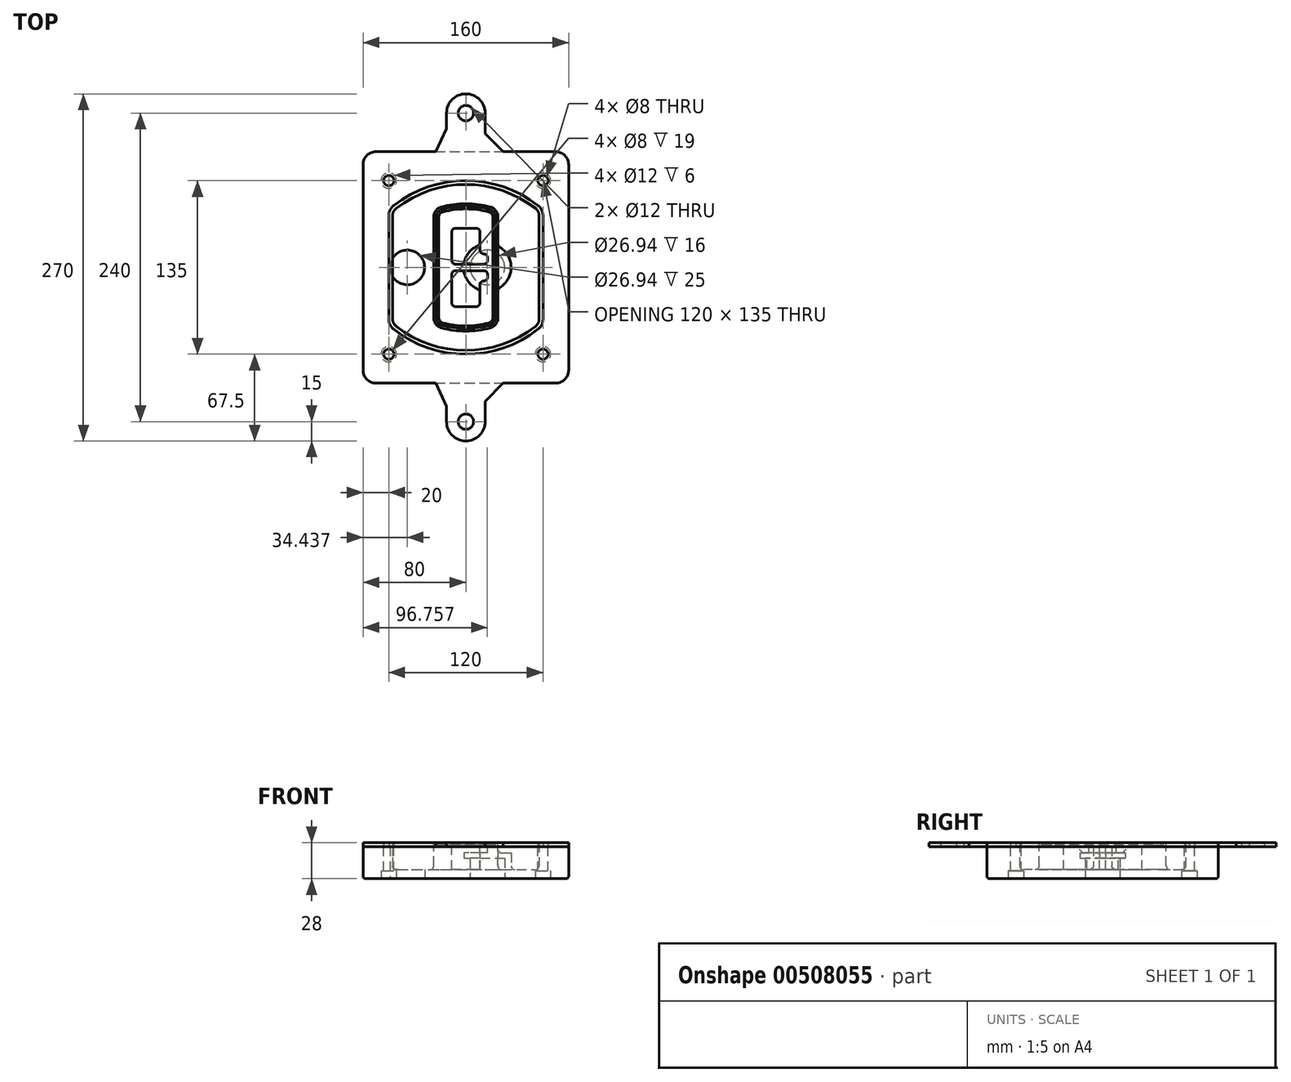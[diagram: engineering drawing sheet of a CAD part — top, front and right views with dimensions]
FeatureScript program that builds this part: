
annotation { "Feature Type Name" : "Feature", "Feature Type Description" : "" }
export const myFeature = defineFeature(function(context is Context, id is Id, definition is map)
    precondition{}
    {
        {
            var Q0;
            Q0=qCreatedBy(makeId("Top.planeOp"),FACE);
            var sketch = newSketch(context, id + "F0", { "sketchPlane" : qUnion([Q0])});
            skPoint(sketch, "E0.rect.middle", {"position": v(0, 0) * mm});
            skLineSegment(sketch, "E1.bottom", {"start": v(-70, -90) * mm, "end": v(70, -90) * mm});
            skLineSegment(sketch, "E1.top", {"start": v(-70, 90) * mm, "end": v(70, 90) * mm});
            skLineSegment(sketch, "E1.left", {"start": v(-80, -80) * mm, "end": v(-80, 80) * mm});
            skLineSegment(sketch, "E1.right", {"start": v(80, -80) * mm, "end": v(80, 80) * mm});
            skLineSegment(sketch, "E2", {"start": v(-80, 90) * mm, "end": v(80, -90) * mm, "construction": true});
            skLineSegment(sketch, "E3", {"start": v(80, 90) * mm, "end": v(-80, -90) * mm, "construction": true});
            skCircle(sketch, "E4", {"center": v(-60, 67.5) * mm, "radius": 4 * mm});
            skCircle(sketch, "E5", {"center": v(60, 67.5) * mm, "radius": 4 * mm});
            skCircle(sketch, "E6", {"center": v(60, -67.5) * mm, "radius": 4 * mm});
            skCircle(sketch, "E7", {"center": v(-60, -67.5) * mm, "radius": 4 * mm});
            skLineSegment(sketch, "E8", {"start": v(-60, 67.5) * mm, "end": v(60, 67.5) * mm, "construction": true});
            skLineSegment(sketch, "E9", {"start": v(60, 67.5) * mm, "end": v(60, -67.5) * mm, "construction": true});
            skLineSegment(sketch, "E10", {"start": v(60, -67.5) * mm, "end": v(-60, -67.5) * mm, "construction": true});
            skLineSegment(sketch, "E11", {"start": v(-60, -67.5) * mm, "end": v(-60, 67.5) * mm, "construction": true});
            skLineSegment(sketch, "E12", {"start": v(-60, 40.3) * mm, "end": v(-60, -40.3) * mm});
            skLineSegment(sketch, "E13", {"start": v(60, 40.3) * mm, "end": v(60, -40.3) * mm});
            skArc(sketch, "E14", {"start": v(56.15, 48.18) * mm, "mid": v(0, 67.5) * mm, "end": v(-56.15, 48.18) * mm});
            skArc(sketch, "E15", {"start": v(-56.15, -48.18) * mm, "mid": v(0, -67.5) * mm, "end": v(56.15, -48.18) * mm});
            skLineSegment(sketch, "E16", {"start": v(-60, 0) * mm, "end": v(60, 0) * mm, "construction": true});
            skPoint(sketch, "E17.visualSharp", {"position": v(-60, -45) * mm});
            skArc(sketch, "E17.filletArc", {"start": v(-60, -40.3) * mm, "mid": v(-58.99, -44.68) * mm, "end": v(-56.15, -48.18) * mm});
            skPoint(sketch, "E18.visualSharp", {"position": v(-60, 45) * mm});
            skArc(sketch, "E18.filletArc", {"start": v(-56.15, 48.18) * mm, "mid": v(-58.99, 44.68) * mm, "end": v(-60, 40.3) * mm});
            skPoint(sketch, "E19.visualSharp", {"position": v(60, 45) * mm});
            skArc(sketch, "E19.filletArc", {"start": v(60, 40.3) * mm, "mid": v(58.99, 44.68) * mm, "end": v(56.15, 48.18) * mm});
            skPoint(sketch, "E20.visualSharp", {"position": v(60, -45) * mm});
            skArc(sketch, "E20.filletArc", {"start": v(56.15, -48.18) * mm, "mid": v(58.99, -44.68) * mm, "end": v(60, -40.3) * mm});
            skPoint(sketch, "E21.visualSharp", {"position": v(-80, 90) * mm});
            skArc(sketch, "E21.filletArc", {"start": v(-70, 90) * mm, "mid": v(-77.07, 87.07) * mm, "end": v(-80, 80) * mm});
            skPoint(sketch, "E22.visualSharp", {"position": v(80, 90) * mm});
            skArc(sketch, "E22.filletArc", {"start": v(80, 80) * mm, "mid": v(77.07, 87.07) * mm, "end": v(70, 90) * mm});
            skPoint(sketch, "E23.visualSharp", {"position": v(80, -90) * mm});
            skArc(sketch, "E23.filletArc", {"start": v(70, -90) * mm, "mid": v(77.07, -87.07) * mm, "end": v(80, -80) * mm});
            skPoint(sketch, "E24.visualSharp", {"position": v(-80, -90) * mm});
            skArc(sketch, "E24.filletArc", {"start": v(-80, -80) * mm, "mid": v(-77.07, -87.07) * mm, "end": v(-70, -90) * mm});
            skArc(sketch, "E25.0", {"start": v(57, 40.3) * mm, "mid": v(56.3, 43.36) * mm, "end": v(54.3, 45.81) * mm});
            skLineSegment(sketch, "E25.1", {"start": v(57, 40.3) * mm, "end": v(57, -40.3) * mm});
            skArc(sketch, "E25.2", {"start": v(54.3, -45.81) * mm, "mid": v(56.3, -43.36) * mm, "end": v(57, -40.3) * mm});
            skArc(sketch, "E25.3", {"start": v(-54.3, -45.81) * mm, "mid": v(0, -64.5) * mm, "end": v(54.3, -45.81) * mm});
            skArc(sketch, "E25.4", {"start": v(-57, -40.3) * mm, "mid": v(-56.3, -43.36) * mm, "end": v(-54.3, -45.81) * mm});
            skArc(sketch, "E25.5", {"start": v(54.3, 45.81) * mm, "mid": v(0, 64.5) * mm, "end": v(-54.3, 45.81) * mm});
            skLineSegment(sketch, "E25.6", {"start": v(-57, 40.3) * mm, "end": v(-57, -40.3) * mm});
            skArc(sketch, "E25.7", {"start": v(-54.3, 45.81) * mm, "mid": v(-56.3, 43.36) * mm, "end": v(-57, 40.3) * mm});
            skArc(sketch, "E26.0", {"start": v(-58.62, 51.33) * mm, "mid": v(-62.58, 46.43) * mm, "end": v(-64, 40.3) * mm});
            skArc(sketch, "E26.1", {"start": v(58.62, 51.33) * mm, "mid": v(0, 71.5) * mm, "end": v(-58.62, 51.33) * mm});
            skArc(sketch, "E26.2", {"start": v(64, 40.3) * mm, "mid": v(62.58, 46.43) * mm, "end": v(58.62, 51.33) * mm});
            skLineSegment(sketch, "E26.3", {"start": v(64, 40.3) * mm, "end": v(64, -40.3) * mm});
            skArc(sketch, "E26.4", {"start": v(58.62, -51.33) * mm, "mid": v(62.58, -46.43) * mm, "end": v(64, -40.3) * mm});
            skLineSegment(sketch, "E26.5", {"start": v(-64, 40.3) * mm, "end": v(-64, -40.3) * mm});
            skArc(sketch, "E26.6", {"start": v(-58.62, -51.33) * mm, "mid": v(0, -71.5) * mm, "end": v(58.62, -51.33) * mm});
            skArc(sketch, "E26.7", {"start": v(-64, -40.3) * mm, "mid": v(-62.58, -46.43) * mm, "end": v(-58.62, -51.33) * mm});
            skSolve(sketch);
        }
        {
            var Q0;
            Q0=makeQuery(id+"F0.imprint","IMPRINT",FACE,{"disambiguationData":[TD([[makeQuery(id+"F0.imprint","IMPRINT",EDGE,{"derivedFrom":sQuery(id+"F0.wireOp",EDGE,"E1.bottom")}),1.0]])]});
            var Q1;
            Q1=makeQuery(id+"F0.imprint","IMPRINT",FACE,{"disambiguationData":[TD([[makeQuery(id+"F0.imprint","IMPRINT",EDGE,{"derivedFrom":sQuery(id+"F0.wireOp",EDGE,"E12")}),1.0]])]});
            var Q2;
            Q2=makeQuery(id+"F0.imprint","IMPRINT",FACE,{"disambiguationData":[TD([[makeQuery(id+"F0.imprint","IMPRINT",EDGE,{"derivedFrom":sQuery(id+"F0.wireOp",EDGE,"E25.0")}),1.0]])]});
            var Q3;
            Q3=makeQuery(id+"F0.imprint","IMPRINT",FACE,{"disambiguationData":[TD([[makeQuery(id+"F0.imprint","IMPRINT",EDGE,{"derivedFrom":sQuery(id+"F0.wireOp",EDGE,"E12")}),-1.0]])]});
            extrude(context, id + "F1", {"entities" : qUnion([Q0, Q1, Q2, Q3]), "oppositeDirection" : true, "depth" : 25 * mm});
        }
        {
            var Q0;
            Q0=makeQuery(id+"F0.imprint","IMPRINT",FACE,{"disambiguationData":[TD([[makeQuery(id+"F0.imprint","IMPRINT",EDGE,{"derivedFrom":sQuery(id+"F0.wireOp",EDGE,"E12")}),1.0]])]});
            extrude(context, id + "F2", {"entities" : qUnion([Q0]), "operationType" : NewBodyOperationType.ADD, "depth" : 3 * mm});
        }
        {
            var Q0;
            Q0=makeQuery(id+"F0.imprint","IMPRINT",FACE,{"disambiguationData":[TD([[makeQuery(id+"F0.imprint","IMPRINT",EDGE,{"derivedFrom":sQuery(id+"F0.wireOp",EDGE,"E25.0")}),1.0]])]});
            extrude(context, id + "F3", {"entities" : qUnion([Q0]), "operationType" : NewBodyOperationType.REMOVE, "oppositeDirection" : true, "depth" : 18 * mm});
        }
        {
            var Q0;
            Q0=makeQuery(id+"F2.opExtrude","CAP_FACE",FACE,{"disambiguationData":[OSD([sQuery(id+"F0.wireOp",EDGE,"E12"),sQuery(id+"F0.wireOp",EDGE,"E13"),sQuery(id+"F0.wireOp",EDGE,"E14"),sQuery(id+"F0.wireOp",EDGE,"E15"),sQuery(id+"F0.wireOp",EDGE,"E17.filletArc"),sQuery(id+"F0.wireOp",EDGE,"E18.filletArc"),sQuery(id+"F0.wireOp",EDGE,"E19.filletArc"),sQuery(id+"F0.wireOp",EDGE,"E20.filletArc"),sQuery(id+"F0.wireOp",EDGE,"E25.0"),sQuery(id+"F0.wireOp",EDGE,"E25.1"),sQuery(id+"F0.wireOp",EDGE,"E25.2"),sQuery(id+"F0.wireOp",EDGE,"E25.3"),sQuery(id+"F0.wireOp",EDGE,"E25.4"),sQuery(id+"F0.wireOp",EDGE,"E25.5"),sQuery(id+"F0.wireOp",EDGE,"E25.6"),sQuery(id+"F0.wireOp",EDGE,"E25.7")])],"isStart":false});
            var sketch = newSketch(context, id + "F4", { "sketchPlane" : qUnion([Q0])});
            skArc(sketch, "E27.0", {"start": v(-19.08, -46.97) * mm, "mid": v(0, -49.5) * mm, "end": v(19.08, -46.97) * mm});
            skArc(sketch, "E28.0", {"start": v(19.08, 46.97) * mm, "mid": v(0, 49.5) * mm, "end": v(-19.08, 46.97) * mm});
            skLineSegment(sketch, "E29", {"start": v(-25, 39.25) * mm, "end": v(-25, -39.25) * mm});
            skLineSegment(sketch, "E30", {"start": v(25, 39.25) * mm, "end": v(25, -39.25) * mm});
            skLineSegment(sketch, "E31", {"start": v(-25, 45.1) * mm, "end": v(25, 45.1) * mm, "construction": true});
            skLineSegment(sketch, "E32", {"start": v(-25, -45.1) * mm, "end": v(25, -45.1) * mm, "construction": true});
            skPoint(sketch, "E33.visualSharp", {"position": v(-25, 45.1) * mm});
            skArc(sketch, "E33.filletArc", {"start": v(-19.08, 46.97) * mm, "mid": v(-23.35, 44.11) * mm, "end": v(-25, 39.25) * mm});
            skPoint(sketch, "E34.visualSharp", {"position": v(25, 45.1) * mm});
            skArc(sketch, "E34.filletArc", {"start": v(25, 39.25) * mm, "mid": v(23.35, 44.11) * mm, "end": v(19.08, 46.97) * mm});
            skPoint(sketch, "E35.visualSharp", {"position": v(25, -45.1) * mm});
            skArc(sketch, "E35.filletArc", {"start": v(19.08, -46.97) * mm, "mid": v(23.35, -44.11) * mm, "end": v(25, -39.25) * mm});
            skPoint(sketch, "E36.visualSharp", {"position": v(-25, -45.1) * mm});
            skArc(sketch, "E36.filletArc", {"start": v(-25, -39.25) * mm, "mid": v(-23.35, -44.11) * mm, "end": v(-19.08, -46.97) * mm});
            skArc(sketch, "E37.0", {"start": v(54.3, 45.81) * mm, "mid": v(0, 64.5) * mm, "end": v(-54.3, 45.81) * mm});
            skArc(sketch, "E37.1", {"start": v(-54.3, 45.81) * mm, "mid": v(-56.3, 43.36) * mm, "end": v(-57, 40.3) * mm});
            skLineSegment(sketch, "E37.2", {"start": v(-57, 40.3) * mm, "end": v(-57, -40.3) * mm});
            skArc(sketch, "E37.3", {"start": v(-57, -40.3) * mm, "mid": v(-56.3, -43.36) * mm, "end": v(-54.3, -45.81) * mm});
            skArc(sketch, "E37.4", {"start": v(-54.3, -45.81) * mm, "mid": v(0, -64.5) * mm, "end": v(54.3, -45.81) * mm});
            skArc(sketch, "E37.5", {"start": v(54.3, -45.81) * mm, "mid": v(56.3, -43.36) * mm, "end": v(57, -40.3) * mm});
            skLineSegment(sketch, "E37.6", {"start": v(57, 40.3) * mm, "end": v(57, -40.3) * mm});
            skArc(sketch, "E37.7", {"start": v(57, 40.3) * mm, "mid": v(56.3, 43.36) * mm, "end": v(54.3, 45.81) * mm});
            skLineSegment(sketch, "E38.0", {"start": v(23, 39.25) * mm, "end": v(23, -39.25) * mm});
            skArc(sketch, "E38.1", {"start": v(18.56, -45.04) * mm, "mid": v(21.76, -42.9) * mm, "end": v(23, -39.25) * mm});
            skArc(sketch, "E38.2", {"start": v(-18.56, -45.04) * mm, "mid": v(0, -47.5) * mm, "end": v(18.56, -45.04) * mm});
            skArc(sketch, "E38.3", {"start": v(-23, -39.25) * mm, "mid": v(-21.76, -42.9) * mm, "end": v(-18.56, -45.04) * mm});
            skLineSegment(sketch, "E38.4", {"start": v(-23, 39.25) * mm, "end": v(-23, -39.25) * mm});
            skArc(sketch, "E38.5", {"start": v(23, 39.25) * mm, "mid": v(21.76, 42.9) * mm, "end": v(18.56, 45.04) * mm});
            skArc(sketch, "E38.6", {"start": v(-18.56, 45.04) * mm, "mid": v(-21.76, 42.9) * mm, "end": v(-23, 39.25) * mm});
            skArc(sketch, "E38.7", {"start": v(18.56, 45.04) * mm, "mid": v(0, 47.5) * mm, "end": v(-18.56, 45.04) * mm});
            skArc(sketch, "E39.0", {"start": v(21, 39.25) * mm, "mid": v(20.18, 41.68) * mm, "end": v(18.04, 43.1) * mm});
            skLineSegment(sketch, "E39.1", {"start": v(21, 39.25) * mm, "end": v(21, -39.25) * mm});
            skArc(sketch, "E39.2", {"start": v(18.04, -43.1) * mm, "mid": v(20.18, -41.68) * mm, "end": v(21, -39.25) * mm});
            skArc(sketch, "E39.3", {"start": v(-18.04, -43.1) * mm, "mid": v(0, -45.5) * mm, "end": v(18.04, -43.1) * mm});
            skArc(sketch, "E39.4", {"start": v(-21, -39.25) * mm, "mid": v(-20.18, -41.68) * mm, "end": v(-18.04, -43.1) * mm});
            skArc(sketch, "E39.5", {"start": v(18.04, 43.1) * mm, "mid": v(0, 45.5) * mm, "end": v(-18.04, 43.1) * mm});
            skLineSegment(sketch, "E39.6", {"start": v(-21, 39.25) * mm, "end": v(-21, -39.25) * mm});
            skArc(sketch, "E39.7", {"start": v(-18.04, 43.1) * mm, "mid": v(-20.18, 41.68) * mm, "end": v(-21, 39.25) * mm});
            skLineSegment(sketch, "E40", {"start": v(-25, 0) * mm, "end": v(25, 0) * mm, "construction": true});
            skLineSegment(sketch, "E41", {"start": v(-11, 5.5) * mm, "end": v(-11, 27.5) * mm});
            skLineSegment(sketch, "E42", {"start": v(-8, 30.5) * mm, "end": v(8, 30.5) * mm});
            skLineSegment(sketch, "E43", {"start": v(11, 27.5) * mm, "end": v(11, 13.5) * mm});
            skLineSegment(sketch, "E44", {"start": v(14, 10.5) * mm, "end": v(14, 10.5) * mm});
            skLineSegment(sketch, "E45", {"start": v(17, 7.5) * mm, "end": v(17, 5.5) * mm});
            skLineSegment(sketch, "E46", {"start": v(14, 2.5) * mm, "end": v(-8, 2.5) * mm});
            skPoint(sketch, "E47.visualSharp", {"position": v(-11, 30.5) * mm});
            skArc(sketch, "E47.filletArc", {"start": v(-8, 30.5) * mm, "mid": v(-10.12, 29.62) * mm, "end": v(-11, 27.5) * mm});
            skPoint(sketch, "E48.visualSharp", {"position": v(11, 30.5) * mm});
            skArc(sketch, "E48.filletArc", {"start": v(11, 27.5) * mm, "mid": v(10.12, 29.62) * mm, "end": v(8, 30.5) * mm});
            skPoint(sketch, "E49.visualSharp", {"position": v(11, 10.5) * mm});
            skArc(sketch, "E49.filletArc", {"start": v(11, 13.5) * mm, "mid": v(11.88, 11.38) * mm, "end": v(14, 10.5) * mm});
            skPoint(sketch, "E50.visualSharp", {"position": v(17, 10.5) * mm});
            skArc(sketch, "E50.filletArc", {"start": v(17, 7.5) * mm, "mid": v(16.12, 9.62) * mm, "end": v(14, 10.5) * mm});
            skPoint(sketch, "E51.visualSharp", {"position": v(17, 2.5) * mm});
            skArc(sketch, "E51.filletArc", {"start": v(14, 2.5) * mm, "mid": v(16.12, 3.38) * mm, "end": v(17, 5.5) * mm});
            skPoint(sketch, "E52.visualSharp", {"position": v(-11, 2.5) * mm});
            skArc(sketch, "E52.filletArc", {"start": v(-11, 5.5) * mm, "mid": v(-10.12, 3.38) * mm, "end": v(-8, 2.5) * mm});
            skLineSegment(sketch, "E53.0.MirrorCS", {"start": v(14, -2.5) * mm, "end": v(-8, -2.5) * mm});
            skArc(sketch, "E54.0.MirrorCS", {"start": v(-11, -5.5) * mm, "mid": v(-10.12, -3.38) * mm, "end": v(-8, -2.5) * mm});
            skLineSegment(sketch, "E55.0.MirrorCS", {"start": v(-11, -5.5) * mm, "end": v(-11, -27.5) * mm});
            skArc(sketch, "E56.0.MirrorCS", {"start": v(-8, -30.5) * mm, "mid": v(-10.12, -29.62) * mm, "end": v(-11, -27.5) * mm});
            skLineSegment(sketch, "E57.0.MirrorCS", {"start": v(-8, -30.5) * mm, "end": v(8, -30.5) * mm});
            skArc(sketch, "E58.0.MirrorCS", {"start": v(11, -27.5) * mm, "mid": v(10.12, -29.62) * mm, "end": v(8, -30.5) * mm});
            skLineSegment(sketch, "E59.0.MirrorCS", {"start": v(11, -27.5) * mm, "end": v(11, -13.5) * mm});
            skArc(sketch, "E60.0.MirrorCS", {"start": v(11, -13.5) * mm, "mid": v(11.88, -11.38) * mm, "end": v(14, -10.5) * mm});
            skArc(sketch, "E61.0.MirrorCS", {"start": v(17, -7.5) * mm, "mid": v(16.12, -9.62) * mm, "end": v(14, -10.5) * mm});
            skLineSegment(sketch, "E62.0.MirrorCS", {"start": v(17, -7.5) * mm, "end": v(17, -5.5) * mm});
            skArc(sketch, "E63.0.MirrorCS", {"start": v(14, -2.5) * mm, "mid": v(16.12, -3.38) * mm, "end": v(17, -5.5) * mm});
            skSolve(sketch);
        }
        {
            var Q0;
            Q0=makeQuery(id+"F4.imprint","IMPRINT",FACE,{"disambiguationData":[TD([[makeQuery(id+"F4.imprint","IMPRINT",EDGE,{"derivedFrom":sQuery(id+"F4.wireOp",EDGE,"E27.0")}),1.0]])]});
            var Q1;
            Q1=makeQuery(id+"F4.imprint","IMPRINT",FACE,{"disambiguationData":[TD([[makeQuery(id+"F4.imprint","IMPRINT",EDGE,{"derivedFrom":sQuery(id+"F4.wireOp",EDGE,"E38.0")}),-1.0]])]});
            var Q2;
            Q2=makeQuery(id+"F4.imprint","IMPRINT",FACE,{"disambiguationData":[TD([[makeQuery(id+"F4.imprint","IMPRINT",EDGE,{"derivedFrom":sQuery(id+"F4.wireOp",EDGE,"E39.0")}),1.0]])]});
            extrude(context, id + "F5", {"entities" : qUnion([Q0, Q1, Q2]), "operationType" : NewBodyOperationType.ADD, "endBound" : BoundingType.UP_TO_NEXT, "oppositeDirection" : true, "depth" : 25 * mm});
        }
        {
            var Q0;
            Q0=makeQuery(id+"F4.imprint","IMPRINT",FACE,{"disambiguationData":[TD([[makeQuery(id+"F4.imprint","IMPRINT",EDGE,{"derivedFrom":sQuery(id+"F4.wireOp",EDGE,"E38.0")}),-1.0]])]});
            extrude(context, id + "F6", {"entities" : qUnion([Q0]), "operationType" : NewBodyOperationType.REMOVE, "oppositeDirection" : true, "depth" : 2 * mm});
        }
        {
            var Q0;
            Q0=makeQuery(id+"F1.opExtrude","CAP_FACE",FACE,{"disambiguationData":[OSD([sQuery(id+"F0.wireOp",EDGE,"E1.bottom"),sQuery(id+"F0.wireOp",EDGE,"E1.top"),sQuery(id+"F0.wireOp",EDGE,"E1.left"),sQuery(id+"F0.wireOp",EDGE,"E1.right"),sQuery(id+"F0.wireOp",EDGE,"E4"),sQuery(id+"F0.wireOp",EDGE,"E5"),sQuery(id+"F0.wireOp",EDGE,"E6"),sQuery(id+"F0.wireOp",EDGE,"E7"),sQuery(id+"F0.wireOp",EDGE,"E21.filletArc"),sQuery(id+"F0.wireOp",EDGE,"E22.filletArc"),sQuery(id+"F0.wireOp",EDGE,"E23.filletArc"),sQuery(id+"F0.wireOp",EDGE,"E24.filletArc")])],"isStart":false});
            var sketch = newSketch(context, id + "F7", { "sketchPlane" : qUnion([Q0])});
            skCircle(sketch, "E64", {"center": v(16.76, 0) * mm, "radius": 13.47 * mm});
            skCircle(sketch, "E65", {"center": v(-45.56, 0) * mm, "radius": 13.47 * mm});
            skLineSegment(sketch, "E66", {"start": v(80, 0) * mm, "end": v(-80, 0) * mm});
            skCircle(sketch, "E67", {"center": v(16.76, 0) * mm, "radius": 18.47 * mm});
            skCircle(sketch, "E68", {"center": v(60, -67.5) * mm, "radius": 6 * mm});
            skCircle(sketch, "E69", {"center": v(-60, -67.5) * mm, "radius": 6 * mm});
            skCircle(sketch, "E70", {"center": v(-60, 67.5) * mm, "radius": 6 * mm});
            skCircle(sketch, "E71", {"center": v(60, 67.5) * mm, "radius": 6 * mm});
            skSolve(sketch);
        }
        {
            var Q0;
            {var subQ1=sQuery(id+"F7.wireOp",EDGE,"E66");var subQ4=sQuery(id+"F7.wireOp",EDGE,"E64");var subQ6=makeQuery(id+"F7.imprint","INTERSECT",VERTEX,{"disambiguationData":[OD(0.0)],"derivedFrom":[subQ4,subQ1]});Q0=makeQuery(id+"F7.imprint","IMPRINT",FACE,{"disambiguationData":[TD([[makeQuery(id+"F7.imprint","IMPRINT",EDGE,{"disambiguationData":[TD([[subQ6,-1.0]])],"derivedFrom":subQ4}),-1.0]])]});}
            var Q1;
            {var subQ0=sQuery(id+"F7.wireOp",EDGE,"E66");var subQ1=sQuery(id+"F7.wireOp",EDGE,"E64");var subQ3=makeQuery(id+"F7.imprint","INTERSECT",VERTEX,{"disambiguationData":[OD(0.0)],"derivedFrom":[subQ1,subQ0]});Q1=makeQuery(id+"F7.imprint","IMPRINT",FACE,{"disambiguationData":[TD([[makeQuery(id+"F7.imprint","IMPRINT",EDGE,{"disambiguationData":[TD([[subQ3,-1.0]])],"derivedFrom":subQ1}),1.0]])]});}
            var Q2;
            {var subQ0=sQuery(id+"F7.wireOp",EDGE,"E66");var subQ1=sQuery(id+"F7.wireOp",EDGE,"E64");var subQ3=makeQuery(id+"F7.imprint","INTERSECT",VERTEX,{"disambiguationData":[OD(0.0)],"derivedFrom":[subQ1,subQ0]});Q2=makeQuery(id+"F7.imprint","IMPRINT",FACE,{"disambiguationData":[TD([[makeQuery(id+"F7.imprint","IMPRINT",EDGE,{"disambiguationData":[TD([[subQ3,1.0]])],"derivedFrom":subQ1}),1.0]])]});}
            var Q3;
            {var subQ1=sQuery(id+"F7.wireOp",EDGE,"E66");var subQ4=sQuery(id+"F7.wireOp",EDGE,"E64");var subQ6=makeQuery(id+"F7.imprint","INTERSECT",VERTEX,{"disambiguationData":[OD(0.0)],"derivedFrom":[subQ4,subQ1]});Q3=makeQuery(id+"F7.imprint","IMPRINT",FACE,{"disambiguationData":[TD([[makeQuery(id+"F7.imprint","IMPRINT",EDGE,{"disambiguationData":[TD([[subQ6,1.0]])],"derivedFrom":subQ4}),-1.0]])]});}
            extrude(context, id + "F8", {"entities" : qUnion([Q0, Q1, Q2, Q3]), "operationType" : NewBodyOperationType.ADD, "oppositeDirection" : true, "depth" : 20 * mm});
        }
        {
            var Q0;
            {var subQ0=sQuery(id+"F7.wireOp",EDGE,"E66");var subQ1=sQuery(id+"F7.wireOp",EDGE,"E64");var subQ3=makeQuery(id+"F7.imprint","INTERSECT",VERTEX,{"disambiguationData":[OD(0.0)],"derivedFrom":[subQ1,subQ0]});Q0=makeQuery(id+"F7.imprint","IMPRINT",FACE,{"disambiguationData":[TD([[makeQuery(id+"F7.imprint","IMPRINT",EDGE,{"disambiguationData":[TD([[subQ3,-1.0]])],"derivedFrom":subQ1}),1.0]])]});}
            var Q1;
            {var subQ0=sQuery(id+"F7.wireOp",EDGE,"E66");var subQ1=sQuery(id+"F7.wireOp",EDGE,"E64");var subQ3=makeQuery(id+"F7.imprint","INTERSECT",VERTEX,{"disambiguationData":[OD(0.0)],"derivedFrom":[subQ1,subQ0]});Q1=makeQuery(id+"F7.imprint","IMPRINT",FACE,{"disambiguationData":[TD([[makeQuery(id+"F7.imprint","IMPRINT",EDGE,{"disambiguationData":[TD([[subQ3,1.0]])],"derivedFrom":subQ1}),1.0]])]});}
            extrude(context, id + "F9", {"entities" : qUnion([Q0, Q1]), "operationType" : NewBodyOperationType.REMOVE, "oppositeDirection" : true, "depth" : 16 * mm});
        }
        {
            var Q0;
            {var subQ0=sQuery(id+"F7.wireOp",EDGE,"E66");var subQ1=sQuery(id+"F7.wireOp",EDGE,"E65");var subQ3=makeQuery(id+"F7.imprint","INTERSECT",VERTEX,{"disambiguationData":[OD(0.0)],"derivedFrom":[subQ1,subQ0]});Q0=makeQuery(id+"F7.imprint","IMPRINT",FACE,{"disambiguationData":[TD([[makeQuery(id+"F7.imprint","IMPRINT",EDGE,{"disambiguationData":[TD([[subQ3,-1.0]])],"derivedFrom":subQ1}),1.0]])]});}
            var Q1;
            {var subQ0=sQuery(id+"F7.wireOp",EDGE,"E66");var subQ1=sQuery(id+"F7.wireOp",EDGE,"E65");var subQ3=makeQuery(id+"F7.imprint","INTERSECT",VERTEX,{"disambiguationData":[OD(0.0)],"derivedFrom":[subQ1,subQ0]});Q1=makeQuery(id+"F7.imprint","IMPRINT",FACE,{"disambiguationData":[TD([[makeQuery(id+"F7.imprint","IMPRINT",EDGE,{"disambiguationData":[TD([[subQ3,1.0]])],"derivedFrom":subQ1}),1.0]])]});}
            extrude(context, id + "F10", {"entities" : qUnion([Q0, Q1]), "operationType" : NewBodyOperationType.REMOVE, "oppositeDirection" : true, "depth" : 25 * mm});
        }
        {
            var Q0;
            Q0=makeQuery(id+"F7.imprint","IMPRINT",FACE,{"disambiguationData":[TD([[makeQuery(id+"F7.imprint","IMPRINT",EDGE,{"derivedFrom":sQuery(id+"F7.wireOp",EDGE,"E68")}),1.0]])]});
            var Q1;
            Q1=makeQuery(id+"F7.imprint","IMPRINT",FACE,{"disambiguationData":[TD([[makeQuery(id+"F7.imprint","IMPRINT",EDGE,{"derivedFrom":makeQuery(id+"F1.opExtrude","CAP_EDGE",EDGE,{"disambiguationData":[OSD([sQuery(id+"F0.wireOp",EDGE,"E5")])],"isStart":false})}),-1.0]])]});
            var Q2;
            Q2=makeQuery(id+"F7.imprint","IMPRINT",FACE,{"disambiguationData":[TD([[makeQuery(id+"F7.imprint","IMPRINT",EDGE,{"derivedFrom":sQuery(id+"F7.wireOp",EDGE,"E69")}),1.0]])]});
            var Q3;
            Q3=makeQuery(id+"F7.imprint","IMPRINT",FACE,{"disambiguationData":[TD([[makeQuery(id+"F7.imprint","IMPRINT",EDGE,{"derivedFrom":makeQuery(id+"F1.opExtrude","CAP_EDGE",EDGE,{"disambiguationData":[OSD([sQuery(id+"F0.wireOp",EDGE,"E4")])],"isStart":false})}),-1.0]])]});
            var Q4;
            Q4=makeQuery(id+"F7.imprint","IMPRINT",FACE,{"disambiguationData":[TD([[makeQuery(id+"F7.imprint","IMPRINT",EDGE,{"derivedFrom":sQuery(id+"F7.wireOp",EDGE,"E70")}),1.0]])]});
            var Q5;
            Q5=makeQuery(id+"F7.imprint","IMPRINT",FACE,{"disambiguationData":[TD([[makeQuery(id+"F7.imprint","IMPRINT",EDGE,{"derivedFrom":makeQuery(id+"F1.opExtrude","CAP_EDGE",EDGE,{"disambiguationData":[OSD([sQuery(id+"F0.wireOp",EDGE,"E7")])],"isStart":false})}),-1.0]])]});
            var Q6;
            Q6=makeQuery(id+"F7.imprint","IMPRINT",FACE,{"disambiguationData":[TD([[makeQuery(id+"F7.imprint","IMPRINT",EDGE,{"derivedFrom":sQuery(id+"F7.wireOp",EDGE,"E71")}),1.0]])]});
            var Q7;
            Q7=makeQuery(id+"F7.imprint","IMPRINT",FACE,{"disambiguationData":[TD([[makeQuery(id+"F7.imprint","IMPRINT",EDGE,{"derivedFrom":makeQuery(id+"F1.opExtrude","CAP_EDGE",EDGE,{"disambiguationData":[OSD([sQuery(id+"F0.wireOp",EDGE,"E6")])],"isStart":false})}),-1.0]])]});
            extrude(context, id + "F11", {"entities" : qUnion([Q0, Q1, Q2, Q3, Q4, Q5, Q6, Q7]), "operationType" : NewBodyOperationType.REMOVE, "oppositeDirection" : true, "depth" : 6 * mm});
        }
        {
            var Q0;
            Q0=makeQuery(id+"F9.boolean.opBoolean","COPY",FACE,{"derivedFrom":makeQuery(id+"F9.opExtrude","CAP_FACE",FACE,{"disambiguationData":[OSD([sQuery(id+"F7.wireOp",EDGE,"E64")])],"isStart":false})});
            var sketch = newSketch(context, id + "F12", { "sketchPlane" : qUnion([Q0])});
            skArc(sketch, "E72.0", {"start": v(11, 17.55) * mm, "mid": v(2.57, 11.82) * mm, "end": v(-1.54, 2.5) * mm});
            skArc(sketch, "E72.1", {"start": v(-1.54, -2.5) * mm, "mid": v(2.57, -11.82) * mm, "end": v(11, -17.55) * mm});
            skLineSegment(sketch, "E73", {"start": v(-1.54, -2.5) * mm, "end": v(14, -2.5) * mm});
            skLineSegment(sketch, "E74.0", {"start": v(14, 2.5) * mm, "end": v(-1.54, 2.5) * mm});
            skArc(sketch, "E74.1", {"start": v(14, 2.5) * mm, "mid": v(16.12, 3.38) * mm, "end": v(17, 5.5) * mm});
            skLineSegment(sketch, "E74.2", {"start": v(17, 7.5) * mm, "end": v(17, 5.5) * mm});
            skArc(sketch, "E74.3", {"start": v(17, 7.5) * mm, "mid": v(16.12, 9.62) * mm, "end": v(14, 10.5) * mm});
            skArc(sketch, "E74.4", {"start": v(11, 13.5) * mm, "mid": v(11.88, 11.38) * mm, "end": v(14, 10.5) * mm});
            skLineSegment(sketch, "E74.5", {"start": v(11, 17.55) * mm, "end": v(11, 13.5) * mm});
            skLineSegment(sketch, "E74.7", {"start": v(14, -2.5) * mm, "end": v(-1.54, -2.5) * mm});
            skArc(sketch, "E74.8", {"start": v(14, -2.5) * mm, "mid": v(16.12, -3.38) * mm, "end": v(17, -5.5) * mm});
            skLineSegment(sketch, "E74.9", {"start": v(17, -7.5) * mm, "end": v(17, -5.5) * mm});
            skArc(sketch, "E74.10", {"start": v(17, -7.5) * mm, "mid": v(16.12, -9.62) * mm, "end": v(14, -10.5) * mm});
            skArc(sketch, "E74.11", {"start": v(11, -13.5) * mm, "mid": v(11.88, -11.38) * mm, "end": v(14, -10.5) * mm});
            skLineSegment(sketch, "E74.12", {"start": v(11, -17.55) * mm, "end": v(11, -13.5) * mm});
            skPoint(sketch, "E75.orphan", {"position": v(11, -27.5) * mm});
            skPoint(sketch, "E76.orphan", {"position": v(-8, -2.5) * mm});
            skPoint(sketch, "E77.orphan", {"position": v(-8, 2.5) * mm});
            skPoint(sketch, "E78.orphan", {"position": v(11, 27.5) * mm});
            skSolve(sketch);
        }
        {
            var Q0;
            {var subQ7=sQuery(id+"F12.wireOp",EDGE,"E72.0");var subQ14=sQuery(id+"F12.wireOp",EDGE,"E72.1");var subQ16=sQuery(id+"F12.wireOp",EDGE,"E74.1");var subQ18=sQuery(id+"F12.wireOp",EDGE,"E74.8");Q0=qUnion([makeQuery(id+"F12.imprint","IMPRINT",FACE,{"disambiguationData":[TD([[makeQuery(id+"F12.imprint","IMPRINT",EDGE,{"derivedFrom":subQ7}),1.0]])]}),makeQuery(id+"F12.imprint","IMPRINT",FACE,{"disambiguationData":[TD([[makeQuery(id+"F12.imprint","IMPRINT",EDGE,{"derivedFrom":subQ14}),1.0]])]}),makeQuery(id+"F12.imprint","IMPRINT",FACE,{"disambiguationData":[TD([[makeQuery(id+"F12.imprint","IMPRINT",EDGE,{"derivedFrom":subQ16}),1.0]])]}),makeQuery(id+"F12.imprint","IMPRINT",FACE,{"disambiguationData":[TD([[makeQuery(id+"F12.imprint","IMPRINT",EDGE,{"derivedFrom":subQ18}),-1.0]])]})]);}
            var Q1;
            Q1=makeQuery(id+"F5.boolean.opBoolean","SPLIT",FACE,{"disambiguationData":[TD([makeQuery(id+"F5.opExtrude","SWEPT_FACE",FACE,{"disambiguationData":[OSD([sQuery(id+"F4.wireOp",EDGE,"E41")])]})])],"derivedFrom":makeQuery(id+"F3.boolean.opBoolean","COPY",FACE,{"derivedFrom":makeQuery(id+"F3.opExtrude","CAP_FACE",FACE,{"disambiguationData":[OSD([sQuery(id+"F0.wireOp",EDGE,"E25.0"),sQuery(id+"F0.wireOp",EDGE,"E25.1"),sQuery(id+"F0.wireOp",EDGE,"E25.2"),sQuery(id+"F0.wireOp",EDGE,"E25.3"),sQuery(id+"F0.wireOp",EDGE,"E25.4"),sQuery(id+"F0.wireOp",EDGE,"E25.5"),sQuery(id+"F0.wireOp",EDGE,"E25.6"),sQuery(id+"F0.wireOp",EDGE,"E25.7")])],"isStart":false})})});
            extrude(context, id + "F13", {"entities" : qUnion([Q0]), "operationType" : NewBodyOperationType.REMOVE, "endBound" : BoundingType.UP_TO_SURFACE, "endBoundEntityFace" : qUnion([Q1]), "depth" : 25 * mm});
        }
        {
            var Q0;
            Q0=makeQuery(id+"F3.boolean.opBoolean","COPY",EDGE,{"derivedFrom":makeQuery(id+"F3.opExtrude","CAP_EDGE",EDGE,{"disambiguationData":[OSD([sQuery(id+"F0.wireOp",EDGE,"E25.6")])],"isStart":false})});
            var Q1;
            Q1=makeQuery(id+"F8.boolean.opBoolean","INTERSECT",EDGE,{"derivedFrom":[makeQuery(id+"F5.opExtrude","SWEPT_FACE",FACE,{"disambiguationData":[OSD([sQuery(id+"F4.wireOp",EDGE,"E30")])]}),makeQuery(id+"F8.opExtrude","CAP_FACE",FACE,{"disambiguationData":[OSD([sQuery(id+"F7.wireOp",EDGE,"E67")])],"isStart":false})]});
            var Q2;
            Q2=makeQuery(id+"F8.boolean.opBoolean","INTERSECT",EDGE,{"disambiguationData":[OD(1.0)],"derivedFrom":[makeQuery(id+"F5.opExtrude","SWEPT_FACE",FACE,{"disambiguationData":[OSD([sQuery(id+"F4.wireOp",EDGE,"E30")])]}),makeQuery(id+"F8.opExtrude","SWEPT_FACE",FACE,{"disambiguationData":[OSD([sQuery(id+"F7.wireOp",EDGE,"E67")])]})]});
            var Q3;
            {var subQ0=sQuery(id+"F4.wireOp",EDGE,"E30");Q3=makeQuery(id+"F8.boolean.opBoolean","SPLIT",EDGE,{"disambiguationData":[TD([makeQuery(id+"F5.opExtrude","SWEPT_FACE",FACE,{"disambiguationData":[OSD([sQuery(id+"F4.wireOp",EDGE,"E35.filletArc")])]})])],"derivedFrom":makeQuery(id+"F5.opExtrude","CAP_EDGE",EDGE,{"disambiguationData":[OSD([subQ0])],"isStart":false})});}
            var Q4;
            {var subQ0=sQuery(id+"F0.wireOp",EDGE,"E25.7");var subQ1=sQuery(id+"F0.wireOp",EDGE,"E25.1");var subQ2=sQuery(id+"F0.wireOp",EDGE,"E25.6");var subQ3=sQuery(id+"F0.wireOp",EDGE,"E25.5");var subQ4=sQuery(id+"F0.wireOp",EDGE,"E25.4");var subQ5=sQuery(id+"F0.wireOp",EDGE,"E25.0");var subQ6=sQuery(id+"F0.wireOp",EDGE,"E25.2");var subQ7=sQuery(id+"F0.wireOp",EDGE,"E25.3");Q4=makeQuery(id+"F8.boolean.opBoolean","INTERSECT",EDGE,{"derivedFrom":[makeQuery(id+"F5.boolean.opBoolean","SPLIT",FACE,{"disambiguationData":[TD([makeQuery(id+"F2.opExtrude","SWEPT_FACE",FACE,{"disambiguationData":[OSD([subQ5])]})])],"derivedFrom":makeQuery(id+"F3.boolean.opBoolean","COPY",FACE,{"derivedFrom":makeQuery(id+"F3.opExtrude","CAP_FACE",FACE,{"disambiguationData":[OSD([subQ5,subQ1,subQ6,subQ7,subQ4,subQ3,subQ2,subQ0])],"isStart":false})})}),makeQuery(id+"F8.opExtrude","SWEPT_FACE",FACE,{"disambiguationData":[OSD([sQuery(id+"F7.wireOp",EDGE,"E67")])]})]});}
            var Q5;
            Q5=makeQuery(id+"F8.boolean.opBoolean","INTERSECT",EDGE,{"disambiguationData":[OD(0.0)],"derivedFrom":[makeQuery(id+"F5.opExtrude","SWEPT_FACE",FACE,{"disambiguationData":[OSD([sQuery(id+"F4.wireOp",EDGE,"E30")])]}),makeQuery(id+"F8.opExtrude","SWEPT_FACE",FACE,{"disambiguationData":[OSD([sQuery(id+"F7.wireOp",EDGE,"E67")])]})]});
            fillet(context, id + "F14", {"entities" : qUnion([Q0, Q1, Q2, Q3, Q4, Q5]), "radius" : 3 * mm, "tangentPropagation" : true, "allowEdgeOverflow" : false});
        }
        {
            var Q0;
            Q0=makeQuery(id+"F1.opExtrude","CAP_EDGE",EDGE,{"disambiguationData":[OSD([sQuery(id+"F0.wireOp",EDGE,"E1.bottom")])],"isStart":false});
            fillet(context, id + "F15", {"entities" : qUnion([Q0]), "radius" : 2 * mm, "tangentPropagation" : true, "allowEdgeOverflow" : false});
        }
        {
            var Q0;
            {var subQ0=sQuery(id+"F0.wireOp",EDGE,"E21.filletArc");var subQ1=sQuery(id+"F0.wireOp",EDGE,"E7");var subQ2=sQuery(id+"F0.wireOp",EDGE,"E6");var subQ3=sQuery(id+"F0.wireOp",EDGE,"E5");var subQ4=sQuery(id+"F0.wireOp",EDGE,"E4");var subQ5=sQuery(id+"F0.wireOp",EDGE,"E22.filletArc");var subQ6=sQuery(id+"F0.wireOp",EDGE,"E1.bottom");var subQ7=sQuery(id+"F0.wireOp",EDGE,"E1.right");var subQ8=sQuery(id+"F0.wireOp",EDGE,"E1.top");var subQ9=sQuery(id+"F0.wireOp",EDGE,"E1.left");var subQ10=sQuery(id+"F0.wireOp",EDGE,"E23.filletArc");var subQ11=sQuery(id+"F0.wireOp",EDGE,"E24.filletArc");Q0=makeQuery(id+"F2.boolean.opBoolean","SPLIT",FACE,{"disambiguationData":[TD([makeQuery(id+"F1.opExtrude","SWEPT_FACE",FACE,{"disambiguationData":[OSD([subQ6])]})])],"derivedFrom":makeQuery(id+"F1.opExtrude","CAP_FACE",FACE,{"disambiguationData":[OSD([subQ6,subQ8,subQ9,subQ7,subQ4,subQ3,subQ2,subQ1,subQ0,subQ5,subQ10,subQ11])],"isStart":true})});}
            var sketch = newSketch(context, id + "F16", { "sketchPlane" : qUnion([Q0])});
            skArc(sketch, "E79.0", {"start": v(-70, 90) * mm, "mid": v(-77.07, 87.07) * mm, "end": v(-80, 80) * mm});
            skLineSegment(sketch, "E79.1", {"start": v(-70, 90) * mm, "end": v(70, 90) * mm});
            skArc(sketch, "E79.2", {"start": v(80, 80) * mm, "mid": v(77.07, 87.07) * mm, "end": v(70, 90) * mm});
            skLineSegment(sketch, "E79.3", {"start": v(80, -80) * mm, "end": v(80, 80) * mm});
            skArc(sketch, "E79.4", {"start": v(70, -90) * mm, "mid": v(77.07, -87.07) * mm, "end": v(80, -80) * mm});
            skLineSegment(sketch, "E79.5", {"start": v(-70, -90) * mm, "end": v(70, -90) * mm});
            skArc(sketch, "E79.6", {"start": v(-80, -80) * mm, "mid": v(-77.07, -87.07) * mm, "end": v(-70, -90) * mm});
            skLineSegment(sketch, "E79.7", {"start": v(-80, -80) * mm, "end": v(-80, 80) * mm});
            skCircle(sketch, "E79.8", {"center": v(-60, 67.5) * mm, "radius": 4 * mm});
            skCircle(sketch, "E79.9", {"center": v(-60, -67.5) * mm, "radius": 4 * mm});
            skCircle(sketch, "E79.10", {"center": v(60, -67.5) * mm, "radius": 4 * mm});
            skCircle(sketch, "E79.11", {"center": v(60, 67.5) * mm, "radius": 4 * mm});
            skArc(sketch, "E79.12", {"start": v(56.15, 48.18) * mm, "mid": v(0, 67.5) * mm, "end": v(-56.15, 48.18) * mm});
            skArc(sketch, "E79.13", {"start": v(60, 40.3) * mm, "mid": v(58.99, 44.68) * mm, "end": v(56.15, 48.18) * mm});
            skLineSegment(sketch, "E79.14", {"start": v(60, 40.3) * mm, "end": v(60, -40.3) * mm});
            skArc(sketch, "E79.15", {"start": v(56.15, -48.18) * mm, "mid": v(58.99, -44.68) * mm, "end": v(60, -40.3) * mm});
            skArc(sketch, "E79.16", {"start": v(-56.15, -48.18) * mm, "mid": v(0, -67.5) * mm, "end": v(56.15, -48.18) * mm});
            skArc(sketch, "E79.17", {"start": v(-60, -40.3) * mm, "mid": v(-58.99, -44.68) * mm, "end": v(-56.15, -48.18) * mm});
            skLineSegment(sketch, "E79.18", {"start": v(-60, 40.3) * mm, "end": v(-60, -40.3) * mm});
            skArc(sketch, "E79.19", {"start": v(-56.15, 48.18) * mm, "mid": v(-58.99, 44.68) * mm, "end": v(-60, 40.3) * mm});
            skLineSegment(sketch, "E80", {"start": v(0, 90) * mm, "end": v(0, 120) * mm, "construction": true});
            skCircle(sketch, "E81", {"center": v(0, 120) * mm, "radius": 6 * mm});
            skLineSegment(sketch, "E82", {"start": v(-15, 120) * mm, "end": v(-15, 108) * mm});
            skLineSegment(sketch, "E83", {"start": v(15, 120) * mm, "end": v(15, 104.09) * mm});
            skArc(sketch, "E84", {"start": v(15, 120) * mm, "mid": v(0, 135) * mm, "end": v(-15, 120) * mm});
            skLineSegment(sketch, "E85", {"start": v(-15, 108) * mm, "end": v(-23.53, 90) * mm});
            skLineSegment(sketch, "E86", {"start": v(15, 104.09) * mm, "end": v(29.09, 90) * mm});
            skLineSegment(sketch, "E87", {"start": v(-80, 0) * mm, "end": v(80, 0) * mm, "construction": true});
            skLineSegment(sketch, "E88.MirrorCS", {"start": v(-15, -108) * mm, "end": v(-23.53, -90) * mm});
            skLineSegment(sketch, "E89.MirrorCS", {"start": v(-15, -120) * mm, "end": v(-15, -108) * mm});
            skArc(sketch, "E90.MirrorCS", {"start": v(15, -120) * mm, "mid": v(0, -135) * mm, "end": v(-15, -120) * mm});
            skCircle(sketch, "E91.MirrorC", {"center": v(0, -120) * mm, "radius": 6 * mm});
            skLineSegment(sketch, "E92.MirrorCS", {"start": v(0, -90) * mm, "end": v(0, -120) * mm, "construction": true});
            skLineSegment(sketch, "E93.MirrorCS", {"start": v(15, -120) * mm, "end": v(15, -104.09) * mm});
            skLineSegment(sketch, "E94.MirrorCS", {"start": v(15, -104.09) * mm, "end": v(29.09, -90) * mm});
            skSolve(sketch);
        }
        {
            var Q0;
            Q0 = qSketchRegion(id + "F16", true);
            var Q1;
            Q1=makeQuery(id+"F2.opExtrude","CAP_FACE",FACE,{"disambiguationData":[OSD([sQuery(id+"F0.wireOp",EDGE,"E12"),sQuery(id+"F0.wireOp",EDGE,"E13"),sQuery(id+"F0.wireOp",EDGE,"E14"),sQuery(id+"F0.wireOp",EDGE,"E15"),sQuery(id+"F0.wireOp",EDGE,"E17.filletArc"),sQuery(id+"F0.wireOp",EDGE,"E18.filletArc"),sQuery(id+"F0.wireOp",EDGE,"E19.filletArc"),sQuery(id+"F0.wireOp",EDGE,"E20.filletArc"),sQuery(id+"F0.wireOp",EDGE,"E25.0"),sQuery(id+"F0.wireOp",EDGE,"E25.1"),sQuery(id+"F0.wireOp",EDGE,"E25.2"),sQuery(id+"F0.wireOp",EDGE,"E25.3"),sQuery(id+"F0.wireOp",EDGE,"E25.4"),sQuery(id+"F0.wireOp",EDGE,"E25.5"),sQuery(id+"F0.wireOp",EDGE,"E25.6"),sQuery(id+"F0.wireOp",EDGE,"E25.7")])],"isStart":false});
            extrude(context, id + "F17", {"entities" : qUnion([Q0]), "endBound" : BoundingType.UP_TO_SURFACE, "endBoundEntityFace" : qUnion([Q1]), "depth" : 25 * mm});
        }
    });
